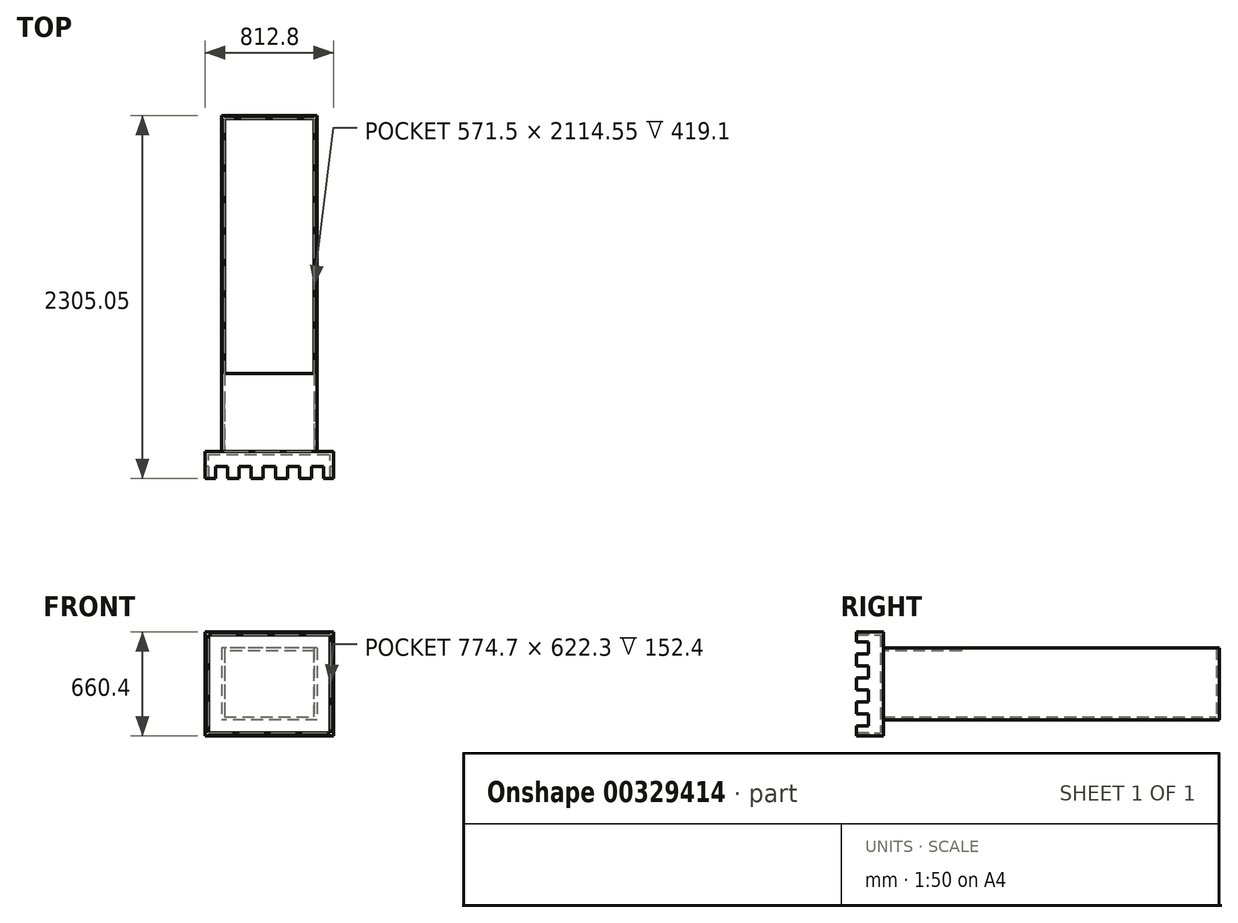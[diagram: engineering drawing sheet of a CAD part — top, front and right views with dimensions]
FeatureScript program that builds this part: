
annotation { "Feature Type Name" : "Feature", "Feature Type Description" : "" }
export const myFeature = defineFeature(function(context is Context, id is Id, definition is map)
    precondition{}
    {
        {
            var Q0;
            Q0=qCreatedBy(makeId("Front.planeOp"),FACE);
            var sketch = newSketch(context, id + "F0", { "sketchPlane" : qUnion([Q0])});
            skLineSegment(sketch, "E0.bottom", {"start": v(304.8, 228.6) * mm, "end": v(285.75, 228.6) * mm});
            skLineSegment(sketch, "E0.top", {"start": v(304.8, -228.6) * mm, "end": v(-304.8, -228.6) * mm});
            skLineSegment(sketch, "E0.left", {"start": v(304.8, 228.6) * mm, "end": v(304.8, -228.6) * mm});
            skLineSegment(sketch, "E0.right", {"start": v(-304.8, 228.6) * mm, "end": v(-304.8, -228.6) * mm});
            skPoint(sketch, "E0.middle", {"position": v(0, 0) * mm});
            skLineSegment(sketch, "E1.top", {"start": v(-285.75, -209.55) * mm, "end": v(285.75, -209.55) * mm});
            skLineSegment(sketch, "E1.left", {"start": v(-285.75, 209.55) * mm, "end": v(-285.75, -209.55) * mm});
            skLineSegment(sketch, "E1.right", {"start": v(285.75, 209.55) * mm, "end": v(285.75, -209.55) * mm});
            skLineSegment(sketch, "E2", {"start": v(-285.75, 209.55) * mm, "end": v(-285.75, 228.6) * mm});
            skLineSegment(sketch, "E3", {"start": v(285.75, 209.55) * mm, "end": v(285.75, 228.6) * mm});
            skLineSegment(sketch, "E4.trimOffspring", {"start": v(-285.75, 228.6) * mm, "end": v(-304.8, 228.6) * mm});
            skSolve(sketch);
        }
        {
            var Q0;
            Q0 = qSketchRegion(id + "F0", true);
            extrude(context, id + "F1", {"entities" : qUnion([Q0]), "endBound" : BoundingType.SYMMETRIC, "depth" : 2133.6 * mm});
        }
        {
            var Q0;
            Q0=makeQuery(id+"F1.opExtrude","CAP_FACE",FACE,{"disambiguationData":[OSD([sQuery(id+"F0.wireOp",EDGE,"E0.bottom"),sQuery(id+"F0.wireOp",EDGE,"E0.top"),sQuery(id+"F0.wireOp",EDGE,"E0.left"),sQuery(id+"F0.wireOp",EDGE,"E0.right"),sQuery(id+"F0.wireOp",EDGE,"E1.top"),sQuery(id+"F0.wireOp",EDGE,"E1.left"),sQuery(id+"F0.wireOp",EDGE,"E1.right"),sQuery(id+"F0.wireOp",EDGE,"E2"),sQuery(id+"F0.wireOp",EDGE,"E3"),sQuery(id+"F0.wireOp",EDGE,"E4.trimOffspring")])],"isStart":false});
            var sketch = newSketch(context, id + "F2", { "sketchPlane" : qUnion([Q0])});
            skLineSegment(sketch, "E5.bottom", {"start": v(-406.4, 330.2) * mm, "end": v(406.4, 330.2) * mm});
            skLineSegment(sketch, "E5.top", {"start": v(-406.4, -330.2) * mm, "end": v(406.4, -330.2) * mm});
            skLineSegment(sketch, "E5.left", {"start": v(-406.4, 330.2) * mm, "end": v(-406.4, -330.2) * mm});
            skLineSegment(sketch, "E5.right", {"start": v(406.4, 330.2) * mm, "end": v(406.4, -330.2) * mm});
            skPoint(sketch, "E5.middle", {"position": v(0, 0) * mm});
            skSolve(sketch);
        }
        {
            var Q0;
            Q0 = qSketchRegion(id + "F2", true);
            extrude(context, id + "F3", {"entities" : qUnion([Q0]), "operationType" : NewBodyOperationType.ADD, "depth" : 19.05 * mm});
        }
        {
            var Q0;
            Q0=makeQuery(id+"F3.opExtrude","CAP_FACE",FACE,{"disambiguationData":[OSD([sQuery(id+"F2.wireOp",EDGE,"E5.bottom"),sQuery(id+"F2.wireOp",EDGE,"E5.top"),sQuery(id+"F2.wireOp",EDGE,"E5.left"),sQuery(id+"F2.wireOp",EDGE,"E5.right")])],"isStart":false});
            var sketch = newSketch(context, id + "F4", { "sketchPlane" : qUnion([Q0])});
            skLineSegment(sketch, "E6.bottom", {"start": v(-406.4, 330.2) * mm, "end": v(406.4, 330.2) * mm});
            skLineSegment(sketch, "E6.top", {"start": v(-406.4, -330.2) * mm, "end": v(406.4, -330.2) * mm});
            skLineSegment(sketch, "E6.left", {"start": v(-406.4, 330.2) * mm, "end": v(-406.4, -330.2) * mm});
            skLineSegment(sketch, "E6.right", {"start": v(406.4, 330.2) * mm, "end": v(406.4, -330.2) * mm});
            skPoint(sketch, "E6.middle", {"position": v(0, 0) * mm});
            skLineSegment(sketch, "E7.bottom", {"start": v(-387.35, 311.15) * mm, "end": v(387.35, 311.15) * mm});
            skLineSegment(sketch, "E7.top", {"start": v(-387.35, -311.15) * mm, "end": v(387.35, -311.15) * mm});
            skLineSegment(sketch, "E7.left", {"start": v(-387.35, 311.15) * mm, "end": v(-387.35, -311.15) * mm});
            skLineSegment(sketch, "E7.right", {"start": v(387.35, 311.15) * mm, "end": v(387.35, -311.15) * mm});
            skSolve(sketch);
        }
        {
            var Q0;
            Q0 = qSketchRegion(id + "F4", true);
            extrude(context, id + "F5", {"entities" : qUnion([Q0]), "operationType" : NewBodyOperationType.ADD, "depth" : 152.4 * mm});
        }
        {
            var Q0;
            Q0=makeQuery(id+"F5.boolean.opBoolean","MERGE",FACE,{"derivedFrom":[makeQuery(id+"F3.opExtrude","SWEPT_FACE",FACE,{"disambiguationData":[OSD([sQuery(id+"F2.wireOp",EDGE,"E5.top")])]}),makeQuery(id+"F5.opExtrude","SWEPT_FACE",FACE,{"disambiguationData":[OSD([sQuery(id+"F4.wireOp",EDGE,"E6.top")])]})]});
            var sketch = newSketch(context, id + "F6", { "sketchPlane" : qUnion([Q0])});
            skLineSegment(sketch, "E8", {"start": v(-406.4, 1238.25) * mm, "end": v(-342.9, 1238.25) * mm, "construction": true});
            skLineSegment(sketch, "E9.bottom", {"start": v(-342.9, 1238.25) * mm, "end": v(-266.7, 1238.25) * mm});
            skLineSegment(sketch, "E9.top", {"start": v(-342.9, 1162.05) * mm, "end": v(-266.7, 1162.05) * mm});
            skLineSegment(sketch, "E9.left", {"start": v(-342.9, 1238.25) * mm, "end": v(-342.9, 1162.05) * mm});
            skLineSegment(sketch, "E9.right", {"start": v(-266.7, 1238.25) * mm, "end": v(-266.7, 1162.05) * mm});
            skLineSegment(sketch, "E10.1.0.0", {"start": v(-114.3, 1238.25) * mm, "end": v(-114.3, 1162.05) * mm});
            skLineSegment(sketch, "E10.1.0.1", {"start": v(-190.5, 1162.05) * mm, "end": v(-114.3, 1162.05) * mm});
            skLineSegment(sketch, "E10.1.0.2", {"start": v(-190.5, 1238.25) * mm, "end": v(-190.5, 1162.05) * mm});
            skLineSegment(sketch, "E10.1.0.3", {"start": v(-190.5, 1238.25) * mm, "end": v(-114.3, 1238.25) * mm});
            skLineSegment(sketch, "E10.2.0.0", {"start": v(38.1, 1238.25) * mm, "end": v(38.1, 1162.05) * mm});
            skLineSegment(sketch, "E10.2.0.1", {"start": v(-38.1, 1162.05) * mm, "end": v(38.1, 1162.05) * mm});
            skLineSegment(sketch, "E10.2.0.2", {"start": v(-38.1, 1238.25) * mm, "end": v(-38.1, 1162.05) * mm});
            skLineSegment(sketch, "E10.2.0.3", {"start": v(-38.1, 1238.25) * mm, "end": v(38.1, 1238.25) * mm});
            skLineSegment(sketch, "E10.3.0.0", {"start": v(190.5, 1238.25) * mm, "end": v(190.5, 1162.05) * mm});
            skLineSegment(sketch, "E10.3.0.1", {"start": v(114.3, 1162.05) * mm, "end": v(190.5, 1162.05) * mm});
            skLineSegment(sketch, "E10.3.0.2", {"start": v(114.3, 1238.25) * mm, "end": v(114.3, 1162.05) * mm});
            skLineSegment(sketch, "E10.3.0.3", {"start": v(114.3, 1238.25) * mm, "end": v(190.5, 1238.25) * mm});
            skLineSegment(sketch, "E10.4.0.0", {"start": v(342.9, 1238.25) * mm, "end": v(342.9, 1162.05) * mm});
            skLineSegment(sketch, "E10.4.0.1", {"start": v(266.7, 1162.05) * mm, "end": v(342.9, 1162.05) * mm});
            skLineSegment(sketch, "E10.4.0.2", {"start": v(266.7, 1238.25) * mm, "end": v(266.7, 1162.05) * mm});
            skLineSegment(sketch, "E10.4.0.3", {"start": v(266.7, 1238.25) * mm, "end": v(342.9, 1238.25) * mm});
            skLineSegment(sketch, "E10.direction1", {"start": v(-342.9, 1162.05) * mm, "end": v(-190.5, 1162.05) * mm, "construction": true});
            skSolve(sketch);
        }
        {
            var Q0;
            Q0 = qSketchRegion(id + "F6", true);
            extrude(context, id + "F7", {"entities" : qUnion([Q0]), "operationType" : NewBodyOperationType.REMOVE, "endBound" : BoundingType.THROUGH_ALL, "oppositeDirection" : true, "depth" : 25.4 * mm});
        }
        {
            var Q0;
            Q0=makeQuery(id+"F5.boolean.opBoolean","MERGE",FACE,{"derivedFrom":[makeQuery(id+"F3.opExtrude","SWEPT_FACE",FACE,{"disambiguationData":[OSD([sQuery(id+"F2.wireOp",EDGE,"E5.left")])]}),makeQuery(id+"F5.opExtrude","SWEPT_FACE",FACE,{"disambiguationData":[OSD([sQuery(id+"F4.wireOp",EDGE,"E6.left")])]})]});
            var sketch = newSketch(context, id + "F8", { "sketchPlane" : qUnion([Q0])});
            skLineSegment(sketch, "E11", {"start": v(1238.25, 330.2) * mm, "end": v(1238.25, 266.7) * mm, "construction": true});
            skLineSegment(sketch, "E12.bottom", {"start": v(1238.25, 266.7) * mm, "end": v(1162.05, 266.7) * mm});
            skLineSegment(sketch, "E12.top", {"start": v(1238.25, 190.5) * mm, "end": v(1162.05, 190.5) * mm});
            skLineSegment(sketch, "E12.left", {"start": v(1238.25, 266.7) * mm, "end": v(1238.25, 190.5) * mm});
            skLineSegment(sketch, "E12.right", {"start": v(1162.05, 266.7) * mm, "end": v(1162.05, 190.5) * mm});
            skLineSegment(sketch, "E13.0.1.0", {"start": v(1162.05, 114.3) * mm, "end": v(1162.05, 38.1) * mm});
            skLineSegment(sketch, "E13.0.1.1", {"start": v(1238.25, 114.3) * mm, "end": v(1162.05, 114.3) * mm});
            skLineSegment(sketch, "E13.0.1.2", {"start": v(1238.25, 114.3) * mm, "end": v(1238.25, 38.1) * mm});
            skLineSegment(sketch, "E13.0.1.3", {"start": v(1238.25, 38.1) * mm, "end": v(1162.05, 38.1) * mm});
            skLineSegment(sketch, "E13.0.2.0", {"start": v(1162.05, -38.1) * mm, "end": v(1162.05, -114.3) * mm});
            skLineSegment(sketch, "E13.0.2.1", {"start": v(1238.25, -38.1) * mm, "end": v(1162.05, -38.1) * mm});
            skLineSegment(sketch, "E13.0.2.2", {"start": v(1238.25, -38.1) * mm, "end": v(1238.25, -114.3) * mm});
            skLineSegment(sketch, "E13.0.2.3", {"start": v(1238.25, -114.3) * mm, "end": v(1162.05, -114.3) * mm});
            skLineSegment(sketch, "E13.0.3.0", {"start": v(1162.05, -190.5) * mm, "end": v(1162.05, -266.7) * mm});
            skLineSegment(sketch, "E13.0.3.1", {"start": v(1238.25, -190.5) * mm, "end": v(1162.05, -190.5) * mm});
            skLineSegment(sketch, "E13.0.3.2", {"start": v(1238.25, -190.5) * mm, "end": v(1238.25, -266.7) * mm});
            skLineSegment(sketch, "E13.0.3.3", {"start": v(1238.25, -266.7) * mm, "end": v(1162.05, -266.7) * mm});
            skLineSegment(sketch, "E13.direction1", {"start": v(1114.3, 190.5) * mm, "end": v(1162.05, 190.5) * mm, "construction": true});
            skLineSegment(sketch, "E13.direction2", {"start": v(1162.05, 190.5) * mm, "end": v(1162.05, 38.1) * mm, "construction": true});
            skSolve(sketch);
        }
        {
            var Q0;
            Q0 = qSketchRegion(id + "F8", true);
            extrude(context, id + "F9", {"entities" : qUnion([Q0]), "operationType" : NewBodyOperationType.REMOVE, "endBound" : BoundingType.THROUGH_ALL, "oppositeDirection" : true, "depth" : 25.4 * mm});
        }
        {
            var Q0;
            Q0=makeQuery(id+"F1.opExtrude","SWEPT_FACE",FACE,{"disambiguationData":[OSD([sQuery(id+"F0.wireOp",EDGE,"E1.top")])]});
            var sketch = newSketch(context, id + "F10", { "sketchPlane" : qUnion([Q0])});
            skLineSegment(sketch, "E14.bottom", {"start": v(285.75, 1066.8) * mm, "end": v(-285.75, 1066.8) * mm});
            skLineSegment(sketch, "E14.top", {"start": v(285.75, 1047.75) * mm, "end": v(-285.75, 1047.75) * mm});
            skLineSegment(sketch, "E14.left", {"start": v(285.75, 1066.8) * mm, "end": v(285.75, 1047.75) * mm});
            skLineSegment(sketch, "E14.right", {"start": v(-285.75, 1066.8) * mm, "end": v(-285.75, 1047.75) * mm});
            skSolve(sketch);
        }
        {
            var Q0;
            Q0 = qSketchRegion(id + "F10", true);
            var Q1;
            Q1=makeQuery(id+"F1.opExtrude","CAP_VERTEX",VERTEX,{"disambiguationData":[OSD([sQuery(id+"F0.wireOp",EDGE,"E0.bottom"),sQuery(id+"F0.wireOp",EDGE,"E3")])],"isStart":true});
            extrude(context, id + "F11", {"entities" : qUnion([Q0]), "operationType" : NewBodyOperationType.ADD, "endBound" : BoundingType.UP_TO_VERTEX, "endBoundEntityVertex" : qUnion([Q1]), "depth" : 285.75 * mm});
        }
        {
            var Q0;
            Q0=makeQuery(id+"F3.opExtrude","CAP_FACE",FACE,{"disambiguationData":[OSD([sQuery(id+"F2.wireOp",EDGE,"E5.bottom"),sQuery(id+"F2.wireOp",EDGE,"E5.top"),sQuery(id+"F2.wireOp",EDGE,"E5.left"),sQuery(id+"F2.wireOp",EDGE,"E5.right")])],"isStart":true});
            var sketch = newSketch(context, id + "F12", { "sketchPlane" : qUnion([Q0])});
            skLineSegment(sketch, "E15.bottom", {"start": v(-285.75, 228.6) * mm, "end": v(285.75, 228.6) * mm});
            skLineSegment(sketch, "E15.top", {"start": v(-285.75, 209.55) * mm, "end": v(285.75, 209.55) * mm});
            skLineSegment(sketch, "E15.left", {"start": v(-285.75, 228.6) * mm, "end": v(-285.75, 209.55) * mm});
            skLineSegment(sketch, "E15.right", {"start": v(285.75, 228.6) * mm, "end": v(285.75, 209.55) * mm});
            skSolve(sketch);
        }
        {
            var Q0;
            Q0 = qSketchRegion(id + "F12", true);
            extrude(context, id + "F13", {"entities" : qUnion([Q0]), "operationType" : NewBodyOperationType.ADD, "depth" : 495.3 * mm});
        }
    });
